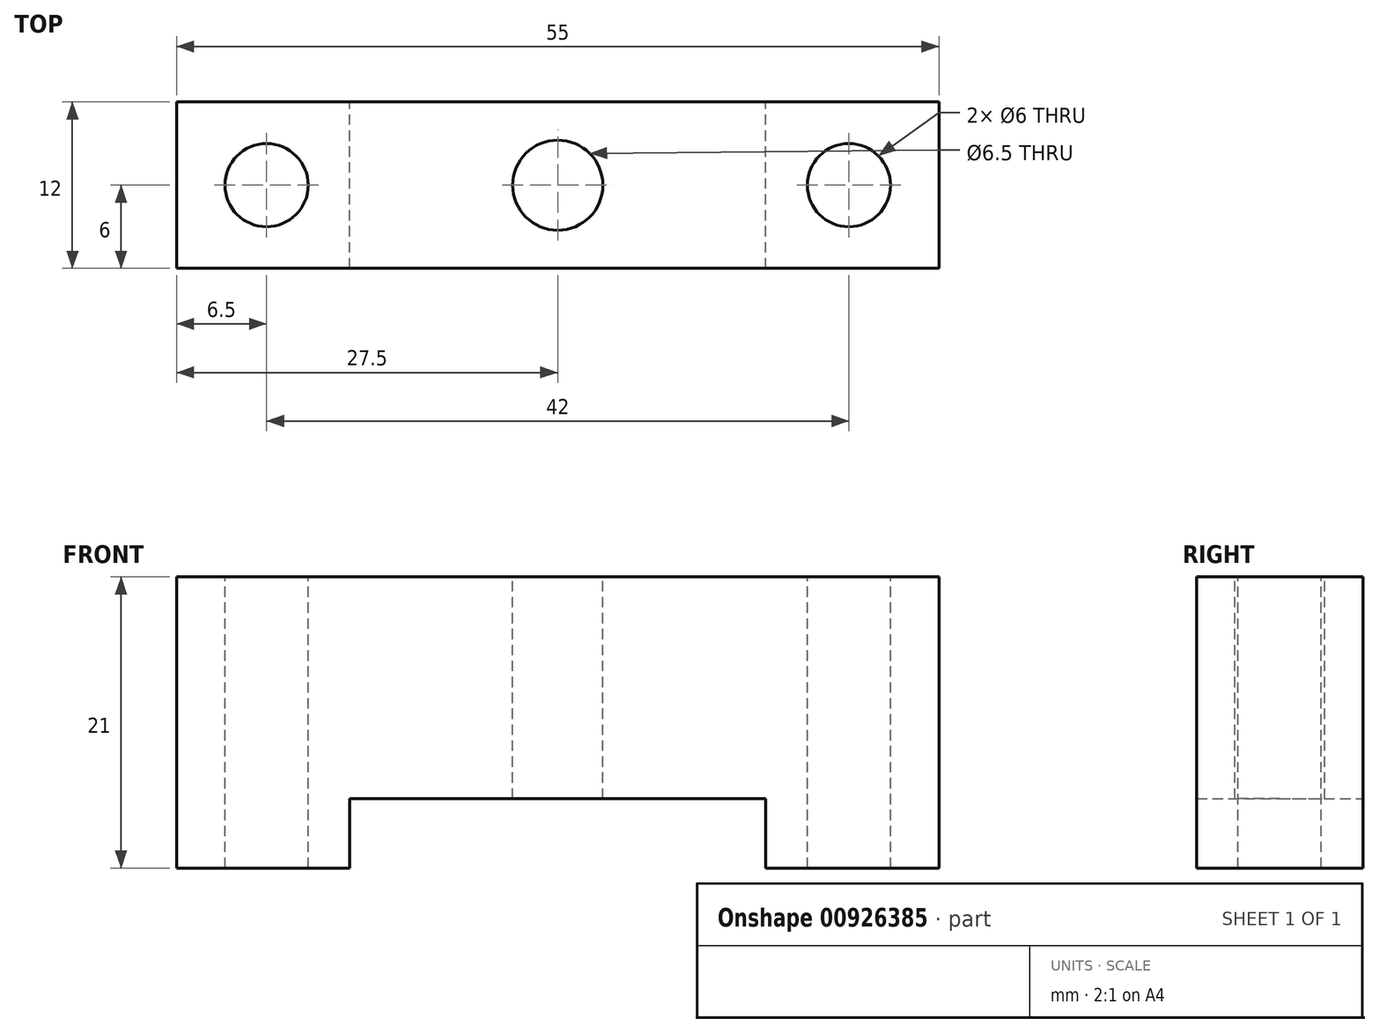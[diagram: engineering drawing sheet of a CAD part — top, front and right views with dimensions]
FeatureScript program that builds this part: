
annotation { "Feature Type Name" : "Feature", "Feature Type Description" : "" }
export const myFeature = defineFeature(function(context is Context, id is Id, definition is map)
    precondition{}
    {
        {
            var Q0;
            Q0=qCreatedBy(makeId("Front.planeOp"),FACE);
            var sketch = newSketch(context, id + "F0", { "sketchPlane" : qUnion([Q0])});
            skLineSegment(sketch, "E0", {"start": v(0, 0) * mm, "end": v(15, 0) * mm});
            skLineSegment(sketch, "E1", {"start": v(15, 0) * mm, "end": v(15, -5) * mm});
            skLineSegment(sketch, "E2", {"start": v(15, -5) * mm, "end": v(27.5, -5) * mm});
            skLineSegment(sketch, "E3", {"start": v(27.5, -5) * mm, "end": v(27.5, 16) * mm});
            skLineSegment(sketch, "E4", {"start": v(27.5, 16) * mm, "end": v(0, 16) * mm});
            skLineSegment(sketch, "E5", {"start": v(0, 16) * mm, "end": v(0, 0) * mm, "construction": true});
            skLineSegment(sketch, "E6.MirrorCS", {"start": v(-27.5, -5) * mm, "end": v(-27.5, 16) * mm});
            skLineSegment(sketch, "E7.MirrorCS", {"start": v(-15, 0) * mm, "end": v(-15, -5) * mm});
            skLineSegment(sketch, "E8.MirrorCS", {"start": v(-15, -5) * mm, "end": v(-27.5, -5) * mm});
            skLineSegment(sketch, "E9.MirrorCS", {"start": v(-27.5, 16) * mm, "end": v(0, 16) * mm});
            skLineSegment(sketch, "E10.MirrorCS", {"start": v(0, 0) * mm, "end": v(-15, 0) * mm});
            skSolve(sketch);
        }
        {
            var Q0;
            Q0=makeQuery(id+"F0.imprint","IMPRINT",FACE,{"disambiguationData":[TD([[makeQuery(id+"F0.imprint","IMPRINT",EDGE,{"derivedFrom":sQuery(id+"F0.wireOp",EDGE,"E0")}),1.0]])]});
            extrude(context, id + "F1", {"entities" : qUnion([Q0]), "depth" : 12 * mm, "offsetDistance" : 25 * mm});
        }
        {
            var Q0;
            Q0=makeQuery(id+"F1.opExtrude","SWEPT_FACE",FACE,{"disambiguationData":[OSD([sQuery(id+"F0.wireOp",EDGE,"E4"),sQuery(id+"F0.wireOp",EDGE,"E9.MirrorCS")])]});
            var sketch = newSketch(context, id + "F2", { "sketchPlane" : qUnion([Q0])});
            skCircle(sketch, "E11", {"center": v(-21, -6) * mm, "radius": 3 * mm});
            skLineSegment(sketch, "E12", {"start": v(0, 0) * mm, "end": v(0, -12) * mm, "construction": true});
            skLineSegment(sketch, "E13", {"start": v(-27.5, -6) * mm, "end": v(27.5, -6) * mm, "construction": true});
            skCircle(sketch, "E14.MirrorC", {"center": v(21, -6) * mm, "radius": 3 * mm});
            skCircle(sketch, "E15", {"center": v(0, -6) * mm, "radius": 3.25 * mm});
            skSolve(sketch);
        }
        {
            var Q0;
            Q0 = qSketchRegion(id + "F2", true);
            extrude(context, id + "F3", {"entities" : qUnion([Q0]), "operationType" : NewBodyOperationType.REMOVE, "endBound" : BoundingType.THROUGH_ALL, "oppositeDirection" : true, "depth" : 25 * mm, "offsetDistance" : 25 * mm});
        }
    });
